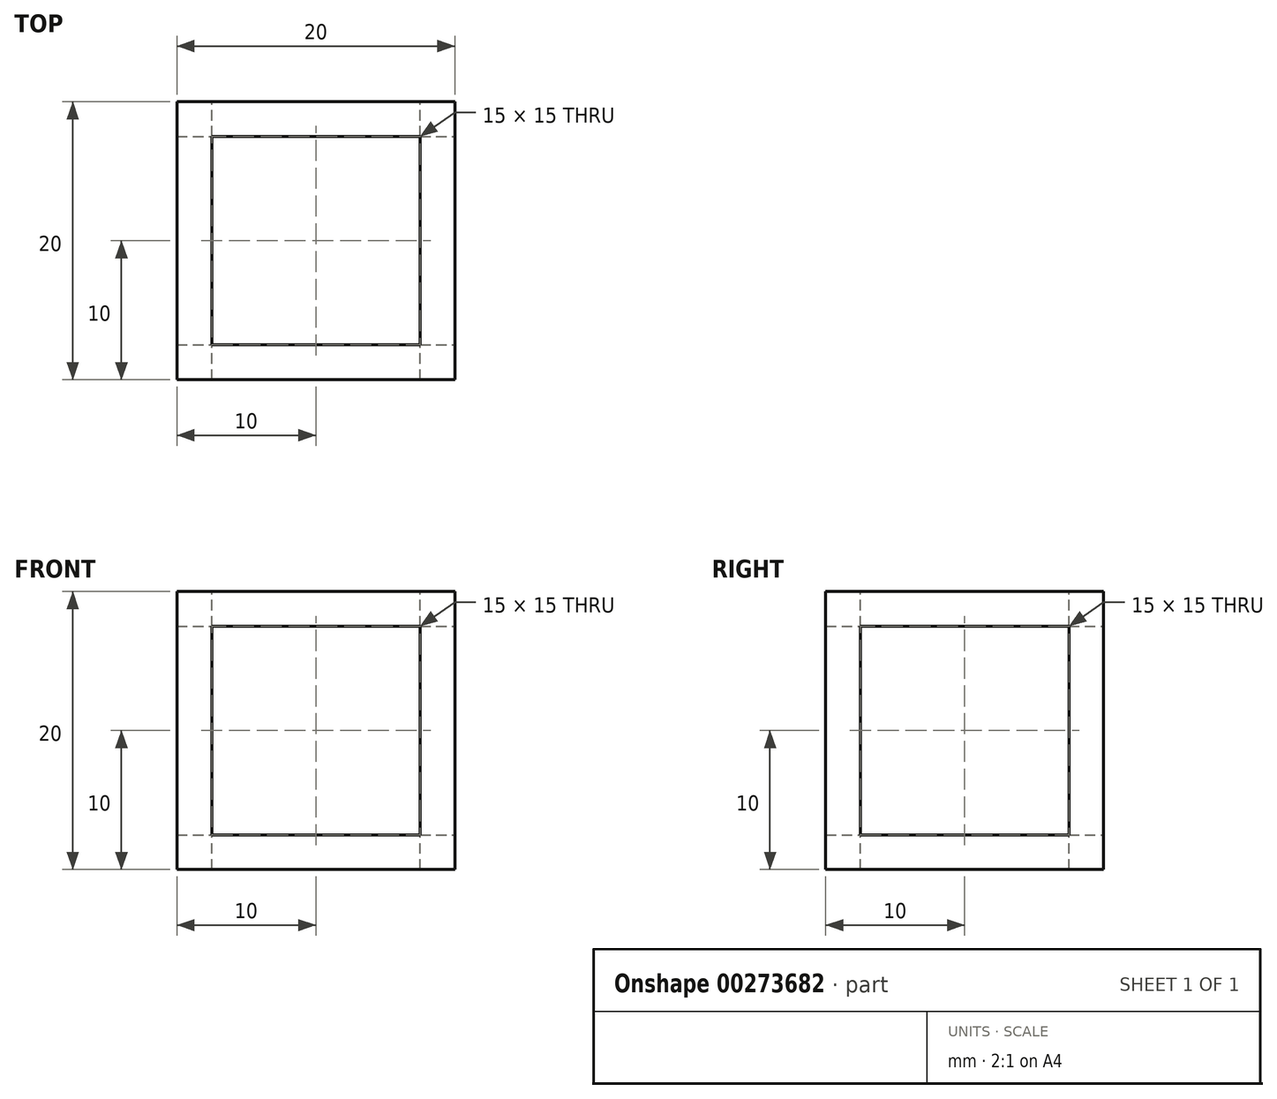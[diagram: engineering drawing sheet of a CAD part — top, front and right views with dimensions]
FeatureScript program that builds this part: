
annotation { "Feature Type Name" : "Feature", "Feature Type Description" : "" }
export const myFeature = defineFeature(function(context is Context, id is Id, definition is map)
    precondition{}
    {
        {
            var Q0;
            Q0=qCreatedBy(makeId("Top.planeOp"),FACE);
            var sketch = newSketch(context, id + "F0", { "sketchPlane" : qUnion([Q0])});
            skLineSegment(sketch, "E0.bottom", {"start": v(0, 0) * mm, "end": v(20, 0) * mm});
            skLineSegment(sketch, "E0.top", {"start": v(0, -20) * mm, "end": v(20, -20) * mm});
            skLineSegment(sketch, "E0.left", {"start": v(0, 0) * mm, "end": v(0, -20) * mm});
            skLineSegment(sketch, "E0.right", {"start": v(20, 0) * mm, "end": v(20, -20) * mm});
            skSolve(sketch);
        }
        {
            var Q0;
            Q0 = qSketchRegion(id + "F0", true);
            extrude(context, id + "F1", {"entities" : qUnion([Q0]), "depth" : 20 * mm});
        }
        {
            var Q0;
            Q0=makeQuery(id+"F1.opExtrude","SWEPT_FACE",FACE,{"disambiguationData":[OSD([sQuery(id+"F0.wireOp",EDGE,"E0.right")])]});
            var sketch = newSketch(context, id + "F2", { "sketchPlane" : qUnion([Q0])});
            skLineSegment(sketch, "E1", {"start": v(-10, 20) * mm, "end": v(-10, 0) * mm});
            skLineSegment(sketch, "E2", {"start": v(0, 10) * mm, "end": v(-20, 10) * mm});
            skLineSegment(sketch, "E3.bottom", {"start": v(-17.5, 2.5) * mm, "end": v(-2.5, 2.5) * mm});
            skLineSegment(sketch, "E3.top", {"start": v(-17.5, 17.5) * mm, "end": v(-2.5, 17.5) * mm});
            skLineSegment(sketch, "E3.left", {"start": v(-17.5, 2.5) * mm, "end": v(-17.5, 17.5) * mm});
            skLineSegment(sketch, "E3.right", {"start": v(-2.5, 2.5) * mm, "end": v(-2.5, 17.5) * mm});
            skPoint(sketch, "E3.middle", {"position": v(-10, 10) * mm});
            skSolve(sketch);
        }
        {
            var Q0;
            {var subQ0=sQuery(id+"F2.wireOp",EDGE,"E3.top");var subQ1=sQuery(id+"F2.wireOp",EDGE,"E1");var subQ2=makeQuery(id+"F2.imprint","INTERSECT",VERTEX,{"derivedFrom":[subQ1,subQ0]});Q0=makeQuery(id+"F2.imprint","IMPRINT",FACE,{"disambiguationData":[TD([[makeQuery(id+"F2.imprint","IMPRINT",EDGE,{"disambiguationData":[TD([[subQ2,-1.0]])],"derivedFrom":subQ1}),1.0]])]});}
            var Q1;
            {var subQ0=sQuery(id+"F2.wireOp",EDGE,"E2");var subQ1=sQuery(id+"F2.wireOp",EDGE,"E1");var subQ2=makeQuery(id+"F2.imprint","INTERSECT",VERTEX,{"derivedFrom":[subQ1,subQ0]});Q1=makeQuery(id+"F2.imprint","IMPRINT",FACE,{"disambiguationData":[TD([[makeQuery(id+"F2.imprint","IMPRINT",EDGE,{"disambiguationData":[TD([[subQ2,-1.0]])],"derivedFrom":subQ1}),1.0]])]});}
            var Q2;
            {var subQ0=sQuery(id+"F2.wireOp",EDGE,"E2");var subQ1=sQuery(id+"F2.wireOp",EDGE,"E1");var subQ2=makeQuery(id+"F2.imprint","INTERSECT",VERTEX,{"derivedFrom":[subQ1,subQ0]});Q2=makeQuery(id+"F2.imprint","IMPRINT",FACE,{"disambiguationData":[TD([[makeQuery(id+"F2.imprint","IMPRINT",EDGE,{"disambiguationData":[TD([[subQ2,-1.0]])],"derivedFrom":subQ1}),-1.0]])]});}
            var Q3;
            {var subQ0=sQuery(id+"F2.wireOp",EDGE,"E3.top");var subQ1=sQuery(id+"F2.wireOp",EDGE,"E1");var subQ2=makeQuery(id+"F2.imprint","INTERSECT",VERTEX,{"derivedFrom":[subQ1,subQ0]});Q3=makeQuery(id+"F2.imprint","IMPRINT",FACE,{"disambiguationData":[TD([[makeQuery(id+"F2.imprint","IMPRINT",EDGE,{"disambiguationData":[TD([[subQ2,-1.0]])],"derivedFrom":subQ1}),-1.0]])]});}
            extrude(context, id + "F3", {"entities" : qUnion([Q0, Q1, Q2, Q3]), "operationType" : NewBodyOperationType.REMOVE, "oppositeDirection" : true, "depth" : 25 * mm});
        }
        {
            var Q0;
            Q0=makeQuery(id+"F1.opExtrude","CAP_FACE",FACE,{"disambiguationData":[OSD([sQuery(id+"F0.wireOp",EDGE,"E0.bottom"),sQuery(id+"F0.wireOp",EDGE,"E0.top"),sQuery(id+"F0.wireOp",EDGE,"E0.left"),sQuery(id+"F0.wireOp",EDGE,"E0.right")])],"isStart":false});
            var sketch = newSketch(context, id + "F4", { "sketchPlane" : qUnion([Q0])});
            skLineSegment(sketch, "E4", {"start": v(10, 0) * mm, "end": v(10, -20) * mm});
            skLineSegment(sketch, "E5", {"start": v(0, -10) * mm, "end": v(20, -10) * mm});
            skLineSegment(sketch, "E6.bottom", {"start": v(17.5, -17.5) * mm, "end": v(2.5, -17.5) * mm});
            skLineSegment(sketch, "E6.top", {"start": v(17.5, -2.5) * mm, "end": v(2.5, -2.5) * mm});
            skLineSegment(sketch, "E6.left", {"start": v(17.5, -17.5) * mm, "end": v(17.5, -2.5) * mm});
            skLineSegment(sketch, "E6.right", {"start": v(2.5, -17.5) * mm, "end": v(2.5, -2.5) * mm});
            skPoint(sketch, "E6.middle", {"position": v(10, -10) * mm});
            skSolve(sketch);
        }
        {
            var Q0;
            {var subQ0=sQuery(id+"F4.wireOp",EDGE,"E6.top");var subQ1=sQuery(id+"F4.wireOp",EDGE,"E4");var subQ2=makeQuery(id+"F4.imprint","INTERSECT",VERTEX,{"derivedFrom":[subQ1,subQ0]});Q0=makeQuery(id+"F4.imprint","IMPRINT",FACE,{"disambiguationData":[TD([[makeQuery(id+"F4.imprint","IMPRINT",EDGE,{"disambiguationData":[TD([[subQ2,-1.0]])],"derivedFrom":subQ1}),1.0]])]});}
            var Q1;
            {var subQ0=sQuery(id+"F4.wireOp",EDGE,"E5");var subQ1=sQuery(id+"F4.wireOp",EDGE,"E4");var subQ2=makeQuery(id+"F4.imprint","INTERSECT",VERTEX,{"derivedFrom":[subQ1,subQ0]});Q1=makeQuery(id+"F4.imprint","IMPRINT",FACE,{"disambiguationData":[TD([[makeQuery(id+"F4.imprint","IMPRINT",EDGE,{"disambiguationData":[TD([[subQ2,-1.0]])],"derivedFrom":subQ1}),-1.0]])]});}
            var Q2;
            {var subQ0=sQuery(id+"F4.wireOp",EDGE,"E5");var subQ1=sQuery(id+"F4.wireOp",EDGE,"E4");var subQ2=makeQuery(id+"F4.imprint","INTERSECT",VERTEX,{"derivedFrom":[subQ1,subQ0]});Q2=makeQuery(id+"F4.imprint","IMPRINT",FACE,{"disambiguationData":[TD([[makeQuery(id+"F4.imprint","IMPRINT",EDGE,{"disambiguationData":[TD([[subQ2,-1.0]])],"derivedFrom":subQ1}),1.0]])]});}
            var Q3;
            {var subQ0=sQuery(id+"F4.wireOp",EDGE,"E6.top");var subQ1=sQuery(id+"F4.wireOp",EDGE,"E4");var subQ2=makeQuery(id+"F4.imprint","INTERSECT",VERTEX,{"derivedFrom":[subQ1,subQ0]});Q3=makeQuery(id+"F4.imprint","IMPRINT",FACE,{"disambiguationData":[TD([[makeQuery(id+"F4.imprint","IMPRINT",EDGE,{"disambiguationData":[TD([[subQ2,-1.0]])],"derivedFrom":subQ1}),-1.0]])]});}
            extrude(context, id + "F5", {"entities" : qUnion([Q0, Q1, Q2, Q3]), "operationType" : NewBodyOperationType.REMOVE, "oppositeDirection" : true, "depth" : 25 * mm});
        }
        {
            var Q0;
            Q0=makeQuery(id+"F1.opExtrude","SWEPT_FACE",FACE,{"disambiguationData":[OSD([sQuery(id+"F0.wireOp",EDGE,"E0.bottom")])]});
            var sketch = newSketch(context, id + "F6", { "sketchPlane" : qUnion([Q0])});
            skLineSegment(sketch, "E7", {"start": v(-10, 0) * mm, "end": v(-10, 20) * mm});
            skLineSegment(sketch, "E8", {"start": v(0, 10) * mm, "end": v(-20, 10) * mm});
            skLineSegment(sketch, "E9.bottom", {"start": v(-17.5, 17.5) * mm, "end": v(-2.5, 17.5) * mm});
            skLineSegment(sketch, "E9.top", {"start": v(-17.5, 2.5) * mm, "end": v(-2.5, 2.5) * mm});
            skLineSegment(sketch, "E9.left", {"start": v(-17.5, 17.5) * mm, "end": v(-17.5, 2.5) * mm});
            skLineSegment(sketch, "E9.right", {"start": v(-2.5, 17.5) * mm, "end": v(-2.5, 2.5) * mm});
            skPoint(sketch, "E9.middle", {"position": v(-10, 10) * mm});
            skSolve(sketch);
        }
        {
            var Q0;
            Q0 = qSketchRegion(id + "F6", true);
            extrude(context, id + "F7", {"entities" : qUnion([Q0]), "operationType" : NewBodyOperationType.REMOVE, "oppositeDirection" : true, "depth" : 25 * mm});
        }
    });
